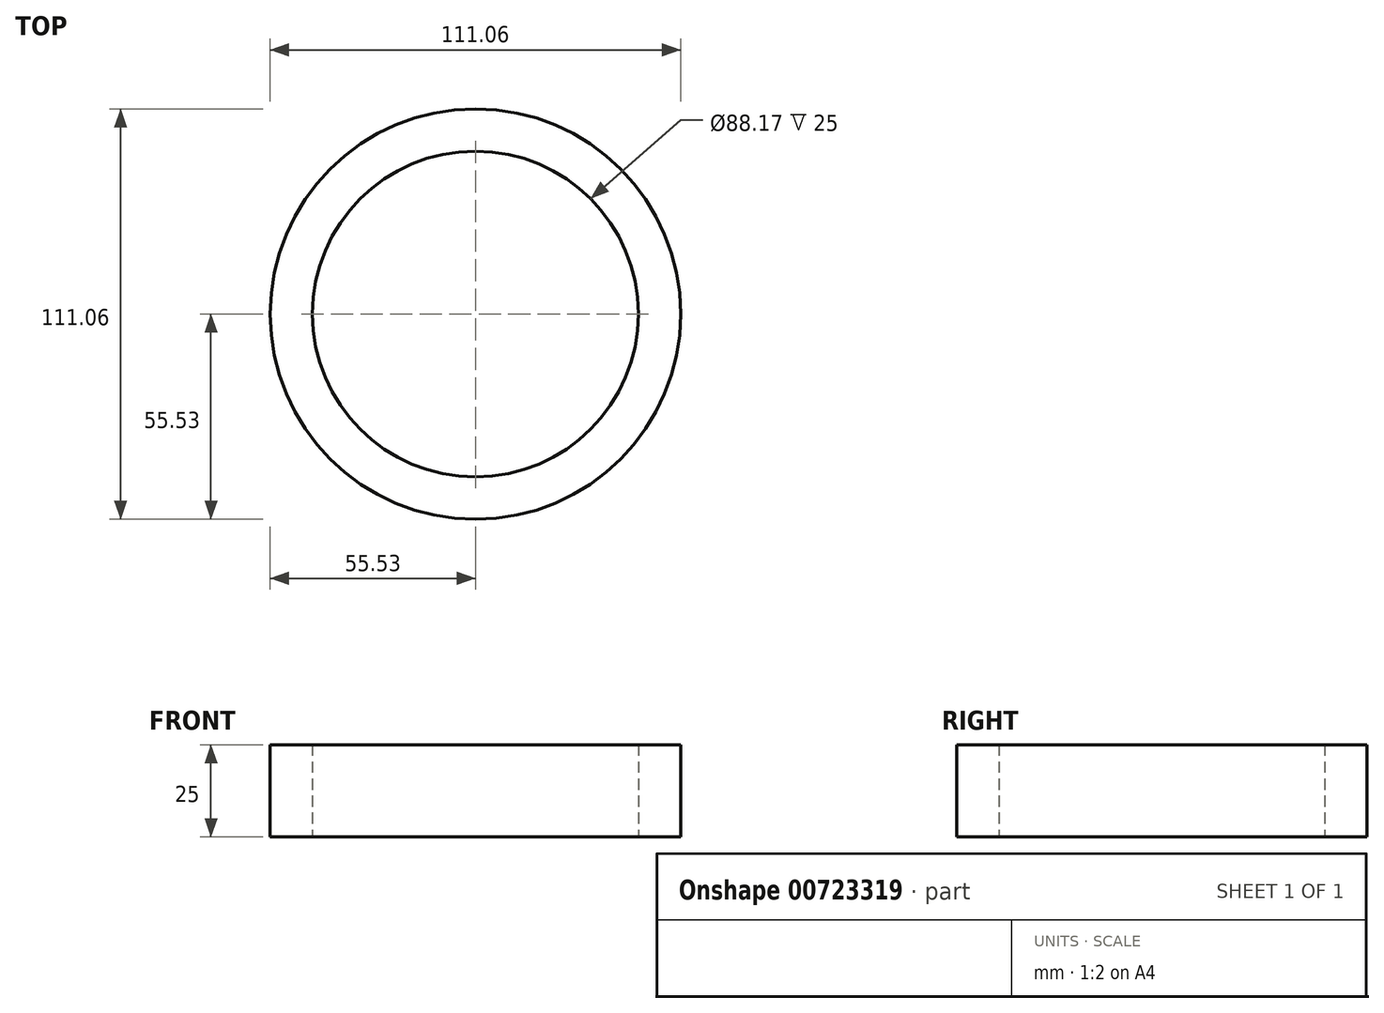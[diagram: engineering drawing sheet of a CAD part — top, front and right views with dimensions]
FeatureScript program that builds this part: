
annotation { "Feature Type Name" : "Feature", "Feature Type Description" : "" }
export const myFeature = defineFeature(function(context is Context, id is Id, definition is map)
    precondition{}
    {
        {
            var Q0;
            Q0=qCreatedBy(makeId("Top.planeOp"),FACE);
            var sketch = newSketch(context, id + "F0", { "sketchPlane" : qUnion([Q0])});
            skCircle(sketch, "E0", {"center": v(0, 0) * mm, "radius": 55.53 * mm});
            skCircle(sketch, "E1", {"center": v(0, 0) * mm, "radius": 44.09 * mm});
            skSolve(sketch);
        }
        {
            var Q0;
            Q0=makeQuery(id+"F0.imprint","IMPRINT",FACE,{"disambiguationData":[TD([[makeQuery(id+"F0.imprint","IMPRINT",EDGE,{"derivedFrom":sQuery(id+"F0.wireOp",EDGE,"E0")}),1.0]])]});
            extrude(context, id + "F1", {"entities" : qUnion([Q0]), "depth" : 25 * mm, "offsetDistance" : 25 * mm});
        }
    });
